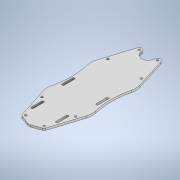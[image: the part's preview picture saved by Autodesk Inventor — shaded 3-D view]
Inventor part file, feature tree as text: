
AUTODESK INVENTOR PART (.ipt)
format: ipt  version: 2020 (Build 240168000, 168)  size: 160,768 bytes
history: native  units: in
note: dims shown in document units (in); Inventor stores cm internally (conversion verified against a paired STEP export)
features: extrude x1, sketch x1
ambient origin geometry x8: Origin, YZ Plane, XZ Plane, XY Plane, X Axis, Y Axis, Z Axis, Center Point
bodies: Solid1 (feature_tree)
feature tree (2):
  extrude  "Extrusion1"  [1 undecoded]
  sketch  "Sketch1"  dims[d0=0.1181in d1=0.0in]
note: 1 required parameter value undecoded (feature->parameter linkage not recoverable at this tier; creation-order binding heuristic only, values carry confidence <= 0.55)
